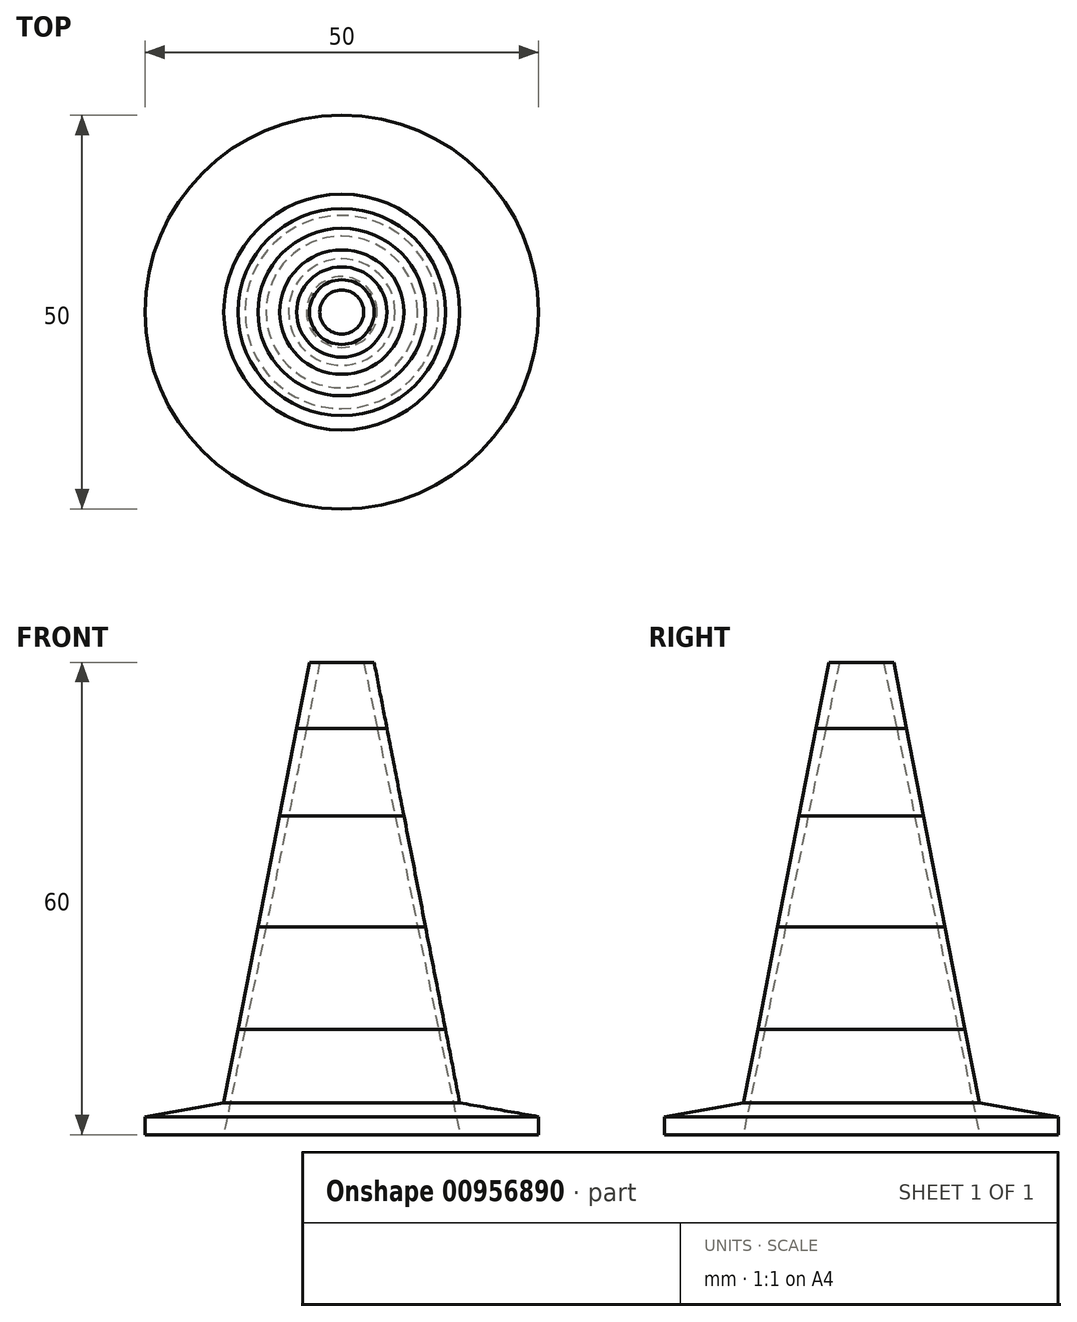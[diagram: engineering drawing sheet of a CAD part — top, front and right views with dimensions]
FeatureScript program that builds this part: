
annotation { "Feature Type Name" : "Feature", "Feature Type Description" : "" }
export const myFeature = defineFeature(function(context is Context, id is Id, definition is map)
    precondition{}
    {
        {
            var Q0;
            Q0=qCreatedBy(makeId("Front.planeOp"),FACE);
            var sketch = newSketch(context, id + "F0", { "sketchPlane" : qUnion([Q0])});
            skLineSegment(sketch, "E0", {"start": v(-25, 0) * mm, "end": v(-25, 2.28) * mm});
            skLineSegment(sketch, "E1", {"start": v(-25, 2.28) * mm, "end": v(-14.98, 4.05) * mm});
            skLineSegment(sketch, "E2", {"start": v(-14.98, 4.05) * mm, "end": v(-4.1, 60) * mm});
            skLineSegment(sketch, "E3", {"start": v(-4.1, 60) * mm, "end": v(0, 60) * mm});
            skLineSegment(sketch, "E4", {"start": v(0, 60) * mm, "end": v(0, 0) * mm});
            skLineSegment(sketch, "E5", {"start": v(0, 0) * mm, "end": v(-25, 0) * mm});
            skLineSegment(sketch, "E6", {"start": v(-13.17, 13.4) * mm, "end": v(0, 13.4) * mm});
            skLineSegment(sketch, "E7", {"start": v(-10.64, 26.4) * mm, "end": v(0, 26.4) * mm});
            skLineSegment(sketch, "E8", {"start": v(-7.9, 40.5) * mm, "end": v(0, 40.5) * mm});
            skPoint(sketch, "E8.endSnap0", {"position": v(0, 30) * mm});
            skLineSegment(sketch, "E9", {"start": v(-5.74, 51.6) * mm, "end": v(0, 51.6) * mm});
            skSolve(sketch);
        }
        {
            var Q0;
            {var subQ0=sQuery(id+"F0.wireOp",EDGE,"E3");Q0=makeQuery(id+"F0.imprint","IMPRINT",FACE,{"disambiguationData":[TD([[makeQuery(id+"F0.imprint","IMPRINT",EDGE,{"derivedFrom":subQ0}),-1.0]])]});}
            var Q1;
            Q1=sQuery(id+"F0.wireOp",EDGE,"E4");
            revolve(context, id + "F1", {"surfaceOperationType" : NewSurfaceOperationType.NEW, "entities" : qUnion([Q0]), "axis" : qUnion([Q1]), "revolveType" : RevolveType.FULL});
        }
        {
            var Q0;
            {var subQ0=sQuery(id+"F0.wireOp",EDGE,"E8");Q0=makeQuery(id+"F0.imprint","IMPRINT",FACE,{"disambiguationData":[TD([[makeQuery(id+"F0.imprint","IMPRINT",EDGE,{"derivedFrom":subQ0}),1.0]])]});}
            var Q1;
            Q1=sQuery(id+"F0.wireOp",EDGE,"E4");
            revolve(context, id + "F2", {"surfaceOperationType" : NewSurfaceOperationType.NEW, "entities" : qUnion([Q0]), "axis" : qUnion([Q1]), "revolveType" : RevolveType.FULL});
        }
        {
            var Q0;
            {var subQ0=sQuery(id+"F0.wireOp",EDGE,"E7");Q0=makeQuery(id+"F0.imprint","IMPRINT",FACE,{"disambiguationData":[TD([[makeQuery(id+"F0.imprint","IMPRINT",EDGE,{"derivedFrom":subQ0}),1.0]])]});}
            var Q1;
            Q1=sQuery(id+"F0.wireOp",EDGE,"E4");
            revolve(context, id + "F3", {"surfaceOperationType" : NewSurfaceOperationType.NEW, "entities" : qUnion([Q0]), "axis" : qUnion([Q1]), "revolveType" : RevolveType.FULL});
        }
        {
            var Q0;
            {var subQ0=sQuery(id+"F0.wireOp",EDGE,"E6");Q0=makeQuery(id+"F0.imprint","IMPRINT",FACE,{"disambiguationData":[TD([[makeQuery(id+"F0.imprint","IMPRINT",EDGE,{"derivedFrom":subQ0}),1.0]])]});}
            var Q1;
            Q1=sQuery(id+"F0.wireOp",EDGE,"E4");
            revolve(context, id + "F4", {"surfaceOperationType" : NewSurfaceOperationType.NEW, "entities" : qUnion([Q0]), "axis" : qUnion([Q1]), "revolveType" : RevolveType.FULL});
        }
        {
            var Q0;
            Q0=makeQuery(id+"F0.imprint","IMPRINT",FACE,{"disambiguationData":[TD([[makeQuery(id+"F0.imprint","IMPRINT",EDGE,{"derivedFrom":sQuery(id+"F0.wireOp",EDGE,"E0")}),-1.0]])]});
            var Q1;
            Q1=sQuery(id+"F0.wireOp",EDGE,"E4");
            revolve(context, id + "F5", {"surfaceOperationType" : NewSurfaceOperationType.NEW, "entities" : qUnion([Q0]), "axis" : qUnion([Q1]), "revolveType" : RevolveType.FULL});
        }
        {
            var Q0;
            Q0=makeQuery(id+"F5.opRevolve","SWEPT_FACE",FACE,{"disambiguationData":[OSD([sQuery(id+"F0.wireOp",EDGE,"E5")])]});
            var sketch = newSketch(context, id + "F6", { "sketchPlane" : qUnion([Q0])});
            skCircle(sketch, "E10", {"center": v(0, 0) * mm, "radius": 15 * mm});
            skSolve(sketch);
        }
        {
            var Q0;
            Q0=makeQuery(id+"F6.imprint","IMPRINT",FACE,{"disambiguationData":[TD([[makeQuery(id+"F6.imprint","IMPRINT",EDGE,{"derivedFrom":sQuery(id+"F6.wireOp",EDGE,"E10")}),1.0]])]});
            extrude(context, id + "F7", {"entities" : qUnion([Q0]), "operationType" : NewBodyOperationType.REMOVE, "endBound" : BoundingType.THROUGH_ALL, "oppositeDirection" : true, "depth" : 25 * mm, "offsetDistance" : 25 * mm, "hasDraft" : true, "draftAngle" : 11.5 * degree, "draftPullDirection" : true});
        }
    });
